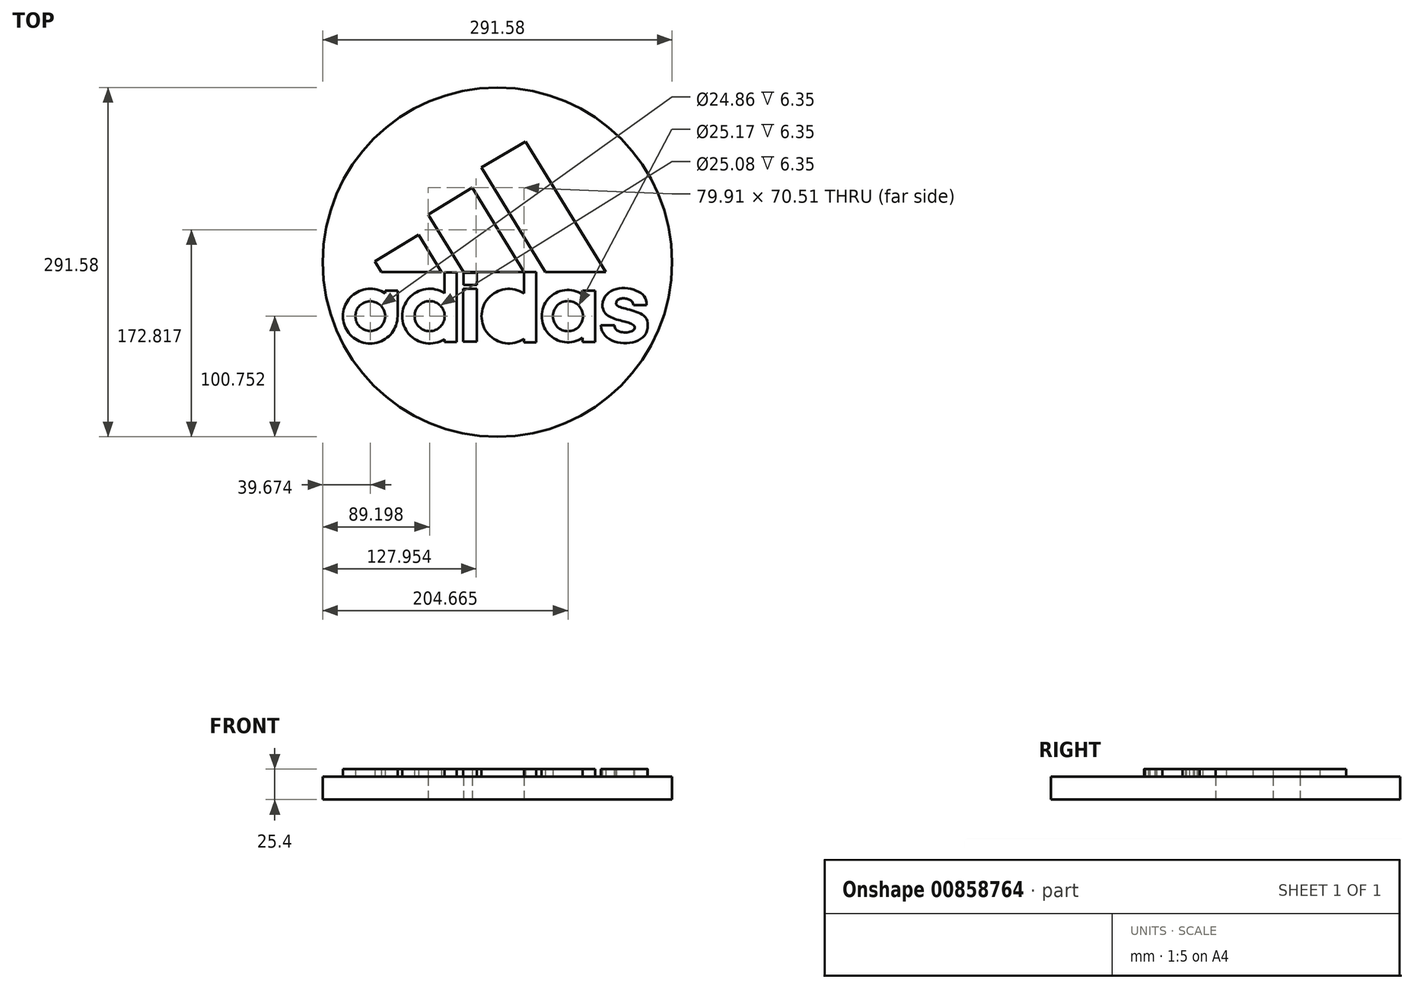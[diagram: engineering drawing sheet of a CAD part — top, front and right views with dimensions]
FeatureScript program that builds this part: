
annotation { "Feature Type Name" : "Feature", "Feature Type Description" : "" }
export const myFeature = defineFeature(function(context is Context, id is Id, definition is map)
    precondition{}
    {
        {
            var Q0;
            Q0=qCreatedBy(makeId("Top.planeOp"),FACE);
            var sketch = newSketch(context, id + "F0", { "sketchPlane" : qUnion([Q0])});
            skLineSegment(sketch, "E0", {"start": v(-124.53, -15.1) * mm, "end": v(-119.06, -24.05) * mm});
            skLineSegment(sketch, "E1", {"start": v(-118.95, -24.22) * mm, "end": v(-119.06, -24.05) * mm});
            skLineSegment(sketch, "E2", {"start": v(-68.76, -24.05) * mm, "end": v(-119.06, -24.05) * mm});
            skLineSegment(sketch, "E3", {"start": v(-124.53, -15.1) * mm, "end": v(-87.93, 7.29) * mm});
            skLineSegment(sketch, "E4", {"start": v(-87.93, 7.29) * mm, "end": v(-68.76, -24.05) * mm});
            skLineSegment(sketch, "E5", {"start": v(-79.93, 24.07) * mm, "end": v(-50.52, -24) * mm});
            skLineSegment(sketch, "E6", {"start": v(-50.52, -24) * mm, "end": v(-0.02, -24) * mm});
            skLineSegment(sketch, "E7", {"start": v(-0.02, -24) * mm, "end": v(-43.15, 46.51) * mm});
            skLineSegment(sketch, "E8", {"start": v(-43.15, 46.51) * mm, "end": v(-79.93, 24.07) * mm});
            skLineSegment(sketch, "E9", {"start": v(-35.45, 63.2) * mm, "end": v(17.91, -24.04) * mm});
            skLineSegment(sketch, "E10", {"start": v(17.91, -24.04) * mm, "end": v(68.17, -24.04) * mm});
            skLineSegment(sketch, "E11", {"start": v(68.17, -24.04) * mm, "end": v(1.42, 85.08) * mm});
            skLineSegment(sketch, "E12", {"start": v(1.42, 85.08) * mm, "end": v(-35.45, 63.2) * mm});
            skCircle(sketch, "E13", {"center": v(-128.26, -60.8) * mm, "radius": 12.43 * mm});
            skCircle(sketch, "E14", {"center": v(-128.26, -60.8) * mm, "radius": 22.79 * mm});
            skLineSegment(sketch, "E15", {"start": v(-115.73, -41.77) * mm, "end": v(-115.73, -39.45) * mm});
            skLineSegment(sketch, "E16", {"start": v(-115.73, -39.45) * mm, "end": v(-105.49, -39.45) * mm});
            skLineSegment(sketch, "E17", {"start": v(-105.49, -39.45) * mm, "end": v(-105.45, -82.16) * mm});
            skLineSegment(sketch, "E18", {"start": v(-105.45, -82.16) * mm, "end": v(-115.55, -82.17) * mm});
            skLineSegment(sketch, "E19", {"start": v(-115.55, -82.17) * mm, "end": v(-115.55, -79.73) * mm});
            skCircle(sketch, "E20", {"center": v(-78.73, -60.8) * mm, "radius": 12.54 * mm});
            skCircle(sketch, "E21", {"center": v(-78.73, -60.8) * mm, "radius": 22.87 * mm});
            skLineSegment(sketch, "E22.bottom", {"start": v(-66.31, -24.2) * mm, "end": v(-56.1, -24.2) * mm});
            skLineSegment(sketch, "E22.top", {"start": v(-66.31, -82.26) * mm, "end": v(-56.1, -82.26) * mm});
            skLineSegment(sketch, "E22.left", {"start": v(-66.31, -24.2) * mm, "end": v(-66.31, -82.26) * mm});
            skLineSegment(sketch, "E22.right", {"start": v(-56.1, -24.2) * mm, "end": v(-56.1, -82.26) * mm});
            skLineSegment(sketch, "E23.bottom", {"start": v(-50.55, -24.72) * mm, "end": v(-39.4, -24.72) * mm});
            skLineSegment(sketch, "E23.top", {"start": v(-50.55, -34.67) * mm, "end": v(-39.4, -34.67) * mm});
            skLineSegment(sketch, "E23.left", {"start": v(-50.55, -24.72) * mm, "end": v(-50.55, -34.67) * mm});
            skLineSegment(sketch, "E23.right", {"start": v(-39.4, -24.72) * mm, "end": v(-39.4, -34.67) * mm});
            skLineSegment(sketch, "E24.bottom", {"start": v(-50.74, -38) * mm, "end": v(-39.28, -38) * mm});
            skLineSegment(sketch, "E24.top", {"start": v(-50.74, -82.23) * mm, "end": v(-39.28, -82.23) * mm});
            skLineSegment(sketch, "E24.left", {"start": v(-50.74, -38) * mm, "end": v(-50.74, -82.23) * mm});
            skLineSegment(sketch, "E24.right", {"start": v(-39.28, -38) * mm, "end": v(-39.28, -82.23) * mm});
            skLineSegment(sketch, "E25.bottom", {"start": v(-0.02, -24) * mm, "end": v(10.31, -24) * mm});
            skLineSegment(sketch, "E25.top", {"start": v(-0.02, -82.56) * mm, "end": v(10.31, -82.56) * mm});
            skLineSegment(sketch, "E25.left", {"start": v(-0.02, -24) * mm, "end": v(-0.02, -82.56) * mm});
            skLineSegment(sketch, "E25.right", {"start": v(10.31, -24) * mm, "end": v(10.31, -82.56) * mm});
            skCircle(sketch, "E26", {"center": v(-12.6, -60.8) * mm, "radius": 12.5 * mm});
            skCircle(sketch, "E27", {"center": v(-12.6, -60.8) * mm, "radius": 22.76 * mm});
            skCircle(sketch, "E28", {"center": v(36.73, -60.8) * mm, "radius": 12.59 * mm});
            skCircle(sketch, "E29", {"center": v(36.73, -60.8) * mm, "radius": 21.9 * mm});
            skLineSegment(sketch, "E30", {"start": v(64.18, -68.27) * mm, "end": v(75.5, -68.27) * mm});
            skFitSpline(sketch, "E31", {"points": [v(64.18, -68.27) * mm, v(103.24, -68.27) * mm], "startDerivative": vector(2.04, -61.1) * mm, "endDerivative": vector(-3.9, 59.95) * mm});
            skFitSpline(sketch, "E32", {"points": [v(103.24, -68.27) * mm, v(77.1, -49.23) * mm], "startDerivative": vector(2.73, 46.2) * mm, "endDerivative": vector(9.73, 22.12) * mm});
            skLineSegment(sketch, "E33", {"start": v(91.36, -51.52) * mm, "end": v(102.2, -51.52) * mm});
            skFitSpline(sketch, "E34", {"points": [v(77.1, -49.23) * mm, v(91.36, -51.52) * mm], "startDerivative": vector(1.57, 14.6) * mm, "endDerivative": vector(1.17, -20.38) * mm});
            skFitSpline(sketch, "E35", {"points": [v(75.5, -68.27) * mm, v(91.39, -68.27) * mm], "startDerivative": vector(-1.46, -27.68) * mm, "endDerivative": vector(-17.8, 21.28) * mm});
            skFitSpline(sketch, "E36", {"points": [v(102.2, -51.52) * mm, v(65.5, -51.52) * mm], "startDerivative": vector(8.48, 47.5) * mm, "endDerivative": vector(-4.1, -64.92) * mm});
            skFitSpline(sketch, "E37", {"points": [v(65.5, -51.52) * mm, v(91.39, -68.27) * mm], "startDerivative": vector(-0.07, -41.2) * mm, "endDerivative": vector(15.27, -13.92) * mm});
            skLineSegment(sketch, "E38.bottom", {"start": v(49.06, -39.47) * mm, "end": v(59.37, -39.47) * mm});
            skLineSegment(sketch, "E38.top", {"start": v(49.06, -82.47) * mm, "end": v(59.37, -82.47) * mm});
            skLineSegment(sketch, "E38.left", {"start": v(49.06, -39.47) * mm, "end": v(49.06, -82.47) * mm});
            skLineSegment(sketch, "E38.right", {"start": v(59.37, -39.47) * mm, "end": v(59.37, -82.47) * mm});
            skSolve(sketch);
        }
        {
            var Q0;
            Q0=qCreatedBy(makeId("Top.planeOp"),FACE);
            var sketch = newSketch(context, id + "F1", { "sketchPlane" : qUnion([Q0])});
            skCircle(sketch, "E39", {"center": v(-22.14, -15.77) * mm, "radius": 145.79 * mm});
            skSolve(sketch);
        }
        {
            var Q0;
            Q0=makeQuery(id+"F0.imprint","IMPRINT",FACE,{"disambiguationData":[TD([[makeQuery(id+"F0.imprint","IMPRINT",EDGE,{"derivedFrom":sQuery(id+"F0.wireOp",EDGE,"E9")}),1.0]])]});
            var Q1;
            Q1=makeQuery(id+"F0.imprint","IMPRINT",FACE,{"disambiguationData":[TD([[makeQuery(id+"F0.imprint","IMPRINT",EDGE,{"derivedFrom":sQuery(id+"F0.wireOp",EDGE,"E5")}),1.0]])]});
            var Q2;
            Q2=makeQuery(id+"F0.imprint","IMPRINT",FACE,{"disambiguationData":[TD([[makeQuery(id+"F0.imprint","IMPRINT",EDGE,{"derivedFrom":sQuery(id+"F0.wireOp",EDGE,"E0")}),1.0]])]});
            var Q3;
            Q3=makeQuery(id+"F0.imprint","IMPRINT",FACE,{"disambiguationData":[TD([[makeQuery(id+"F0.imprint","IMPRINT",EDGE,{"derivedFrom":sQuery(id+"F0.wireOp",EDGE,"E13")}),-1.0]])]});
            var Q4;
            {var subQ0=sQuery(id+"F0.wireOp",EDGE,"E15");Q4=makeQuery(id+"F0.imprint","IMPRINT",FACE,{"disambiguationData":[TD([[makeQuery(id+"F0.imprint","IMPRINT",EDGE,{"derivedFrom":subQ0}),-1.0]])]});}
            var Q5;
            {var subQ0=sQuery(id+"F0.wireOp",EDGE,"E22.left");var subQ1=sQuery(id+"F0.wireOp",EDGE,"E20");var subQ2=makeQuery(id+"F0.imprint","INTERSECT",VERTEX,{"disambiguationData":[OD(0.0)],"derivedFrom":[subQ1,subQ0]});Q5=makeQuery(id+"F0.imprint","IMPRINT",FACE,{"disambiguationData":[TD([[makeQuery(id+"F0.imprint","IMPRINT",EDGE,{"disambiguationData":[TD([[subQ2,-1.0]])],"derivedFrom":subQ1}),-1.0]])]});}
            var Q6;
            {var subQ5=sQuery(id+"F0.wireOp",EDGE,"E22.bottom");Q6=makeQuery(id+"F0.imprint","IMPRINT",FACE,{"disambiguationData":[TD([[makeQuery(id+"F0.imprint","IMPRINT",EDGE,{"derivedFrom":subQ5}),-1.0]])]});}
            var Q7;
            {var subQ5=sQuery(id+"F0.wireOp",EDGE,"E22.top");Q7=makeQuery(id+"F0.imprint","IMPRINT",FACE,{"disambiguationData":[TD([[makeQuery(id+"F0.imprint","IMPRINT",EDGE,{"derivedFrom":subQ5}),1.0]])]});}
            var Q8;
            {var subQ0=sQuery(id+"F0.wireOp",EDGE,"E22.left");var subQ3=sQuery(id+"F0.wireOp",EDGE,"E20");var subQ4=makeQuery(id+"F0.imprint","INTERSECT",VERTEX,{"disambiguationData":[OD(0.0)],"derivedFrom":[subQ3,subQ0]});Q8=makeQuery(id+"F0.imprint","IMPRINT",FACE,{"disambiguationData":[TD([[makeQuery(id+"F0.imprint","IMPRINT",EDGE,{"disambiguationData":[TD([[subQ4,1.0]])],"derivedFrom":subQ3}),-1.0]])]});}
            var Q9;
            Q9=makeQuery(id+"F0.imprint","IMPRINT",FACE,{"disambiguationData":[TD([[makeQuery(id+"F0.imprint","IMPRINT",EDGE,{"derivedFrom":sQuery(id+"F0.wireOp",EDGE,"E24.bottom")}),-1.0]])]});
            var Q10;
            Q10=makeQuery(id+"F0.imprint","IMPRINT",FACE,{"disambiguationData":[TD([[makeQuery(id+"F0.imprint","IMPRINT",EDGE,{"derivedFrom":sQuery(id+"F0.wireOp",EDGE,"E23.bottom")}),-1.0]])]});
            var Q11;
            Q11=makeQuery(id+"F0.imprint","IMPRINT",FACE,{"disambiguationData":[TD([[makeQuery(id+"F0.imprint","IMPRINT",EDGE,{"derivedFrom":sQuery(id+"F0.wireOp",EDGE,"E26")}),1.0]])]});
            var Q12;
            Q12=makeQuery(id+"F0.imprint","IMPRINT",FACE,{"disambiguationData":[TD([[makeQuery(id+"F0.imprint","IMPRINT",EDGE,{"derivedFrom":sQuery(id+"F0.wireOp",EDGE,"E26")}),-1.0]])]});
            var Q13;
            {var subQ0=sQuery(id+"F0.wireOp",EDGE,"E27");var subQ1=sQuery(id+"F0.wireOp",EDGE,"E25.left");var subQ2=makeQuery(id+"F0.imprint","INTERSECT",VERTEX,{"disambiguationData":[OD(0.0)],"derivedFrom":[subQ1,subQ0]});Q13=makeQuery(id+"F0.imprint","IMPRINT",FACE,{"disambiguationData":[TD([[makeQuery(id+"F0.imprint","IMPRINT",EDGE,{"disambiguationData":[TD([[subQ2,-1.0]])],"derivedFrom":subQ1}),1.0]])]});}
            var Q14;
            {var subQ4=sQuery(id+"F0.wireOp",EDGE,"E25.bottom");Q14=makeQuery(id+"F0.imprint","IMPRINT",FACE,{"disambiguationData":[TD([[makeQuery(id+"F0.imprint","IMPRINT",EDGE,{"derivedFrom":subQ4}),-1.0]])]});}
            var Q15;
            {var subQ0=sQuery(id+"F0.wireOp",EDGE,"E38.left");var subQ1=sQuery(id+"F0.wireOp",EDGE,"E28");var subQ2=makeQuery(id+"F0.imprint","INTERSECT",VERTEX,{"disambiguationData":[OD(0.0)],"derivedFrom":[subQ1,subQ0]});Q15=makeQuery(id+"F0.imprint","IMPRINT",FACE,{"disambiguationData":[TD([[makeQuery(id+"F0.imprint","IMPRINT",EDGE,{"disambiguationData":[TD([[subQ2,1.0]])],"derivedFrom":subQ1}),-1.0]])]});}
            var Q16;
            {var subQ0=sQuery(id+"F0.wireOp",EDGE,"E38.left");var subQ1=sQuery(id+"F0.wireOp",EDGE,"E28");var subQ2=makeQuery(id+"F0.imprint","INTERSECT",VERTEX,{"disambiguationData":[OD(0.0)],"derivedFrom":[subQ1,subQ0]});Q16=makeQuery(id+"F0.imprint","IMPRINT",FACE,{"disambiguationData":[TD([[makeQuery(id+"F0.imprint","IMPRINT",EDGE,{"disambiguationData":[TD([[subQ2,-1.0]])],"derivedFrom":subQ1}),-1.0]])]});}
            var Q17;
            {var subQ1=sQuery(id+"F0.wireOp",EDGE,"E38.bottom");Q17=makeQuery(id+"F0.imprint","IMPRINT",FACE,{"disambiguationData":[TD([[makeQuery(id+"F0.imprint","IMPRINT",EDGE,{"derivedFrom":subQ1}),-1.0]])]});}
            var Q18;
            Q18=makeQuery(id+"F0.imprint","IMPRINT",FACE,{"disambiguationData":[TD([[makeQuery(id+"F0.imprint","IMPRINT",EDGE,{"derivedFrom":sQuery(id+"F0.wireOp",EDGE,"E30")}),-1.0]])]});
            extrude(context, id + "F2", {"entities" : qUnion([Q0, Q1, Q2, Q3, Q4, Q5, Q6, Q7, Q8, Q9, Q10, Q11, Q12, Q13, Q14, Q15, Q16, Q17, Q18]), "depth" : 25.4 * mm, "offsetDistance" : 25.4 * mm});
        }
        {
            var Q0;
            Q0=makeQuery(id+"F1.imprint","IMPRINT",FACE,{"disambiguationData":[TD([[makeQuery(id+"F1.imprint","IMPRINT",EDGE,{"derivedFrom":sQuery(id+"F1.wireOp",EDGE,"E39")}),1.0]])]});
            extrude(context, id + "F3", {"entities" : qUnion([Q0]), "operationType" : NewBodyOperationType.ADD, "depth" : 19.05 * mm, "offsetDistance" : 25.4 * mm});
        }
    });
